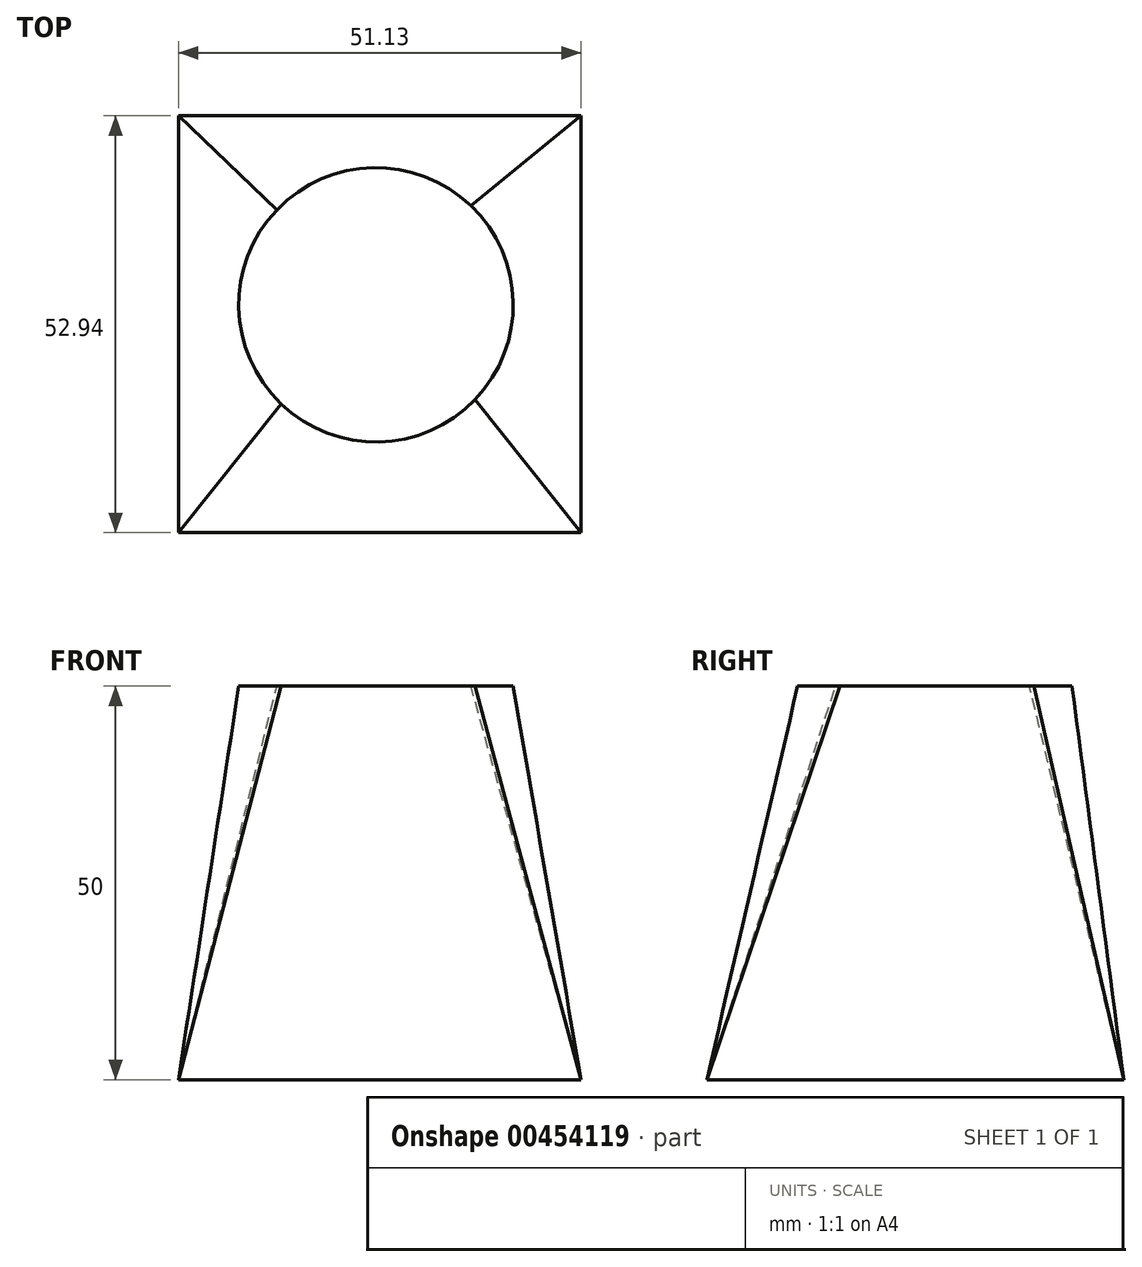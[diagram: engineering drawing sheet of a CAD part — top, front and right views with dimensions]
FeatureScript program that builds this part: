
annotation { "Feature Type Name" : "Feature", "Feature Type Description" : "" }
export const myFeature = defineFeature(function(context is Context, id is Id, definition is map)
    precondition{}
    {
        {
            var Q0;
            Q0=qCreatedBy(makeId("Top.planeOp"),FACE);
            var sketch = newSketch(context, id + "F0", { "sketchPlane" : qUnion([Q0])});
            skLineSegment(sketch, "E0.bottom", {"start": v(0, 0) * mm, "end": v(51.13, 0) * mm});
            skLineSegment(sketch, "E0.top", {"start": v(0, -52.94) * mm, "end": v(51.13, -52.94) * mm});
            skLineSegment(sketch, "E0.left", {"start": v(0, 0) * mm, "end": v(0, -52.94) * mm});
            skLineSegment(sketch, "E0.right", {"start": v(51.13, 0) * mm, "end": v(51.13, -52.94) * mm});
            skSolve(sketch);
        }
        {
            var Q0;
            Q0=qCreatedBy(makeId("Top.planeOp"),FACE);
            cPlane(context, id + "F1", {"entities" : qUnion([Q0]), "cplaneType" : CPlaneType.OFFSET, "offset" : 50 * mm, "width" : 150 * mm, "height" : 150 * mm});
        }
        {
            var Q0;
            Q0=qCreatedBy(id+"F1.planeOp",FACE);
            var sketch = newSketch(context, id + "F2", { "sketchPlane" : qUnion([Q0])});
            skCircle(sketch, "E1", {"center": v(25.08, -24) * mm, "radius": 17.43 * mm});
            skSolve(sketch);
        }
        {
            var Q0;
            Q0 = qSketchRegion(id + "F0", true);
            var Q1;
            Q1 = qSketchRegion(id + "F2", true);
            loft(context, id + "F3", {"sheetProfilesArray" : [{ "sheetProfileEntities" : qUnion([Q0]) }, { "sheetProfileEntities" : qUnion([Q1]) }]});
        }
    });
